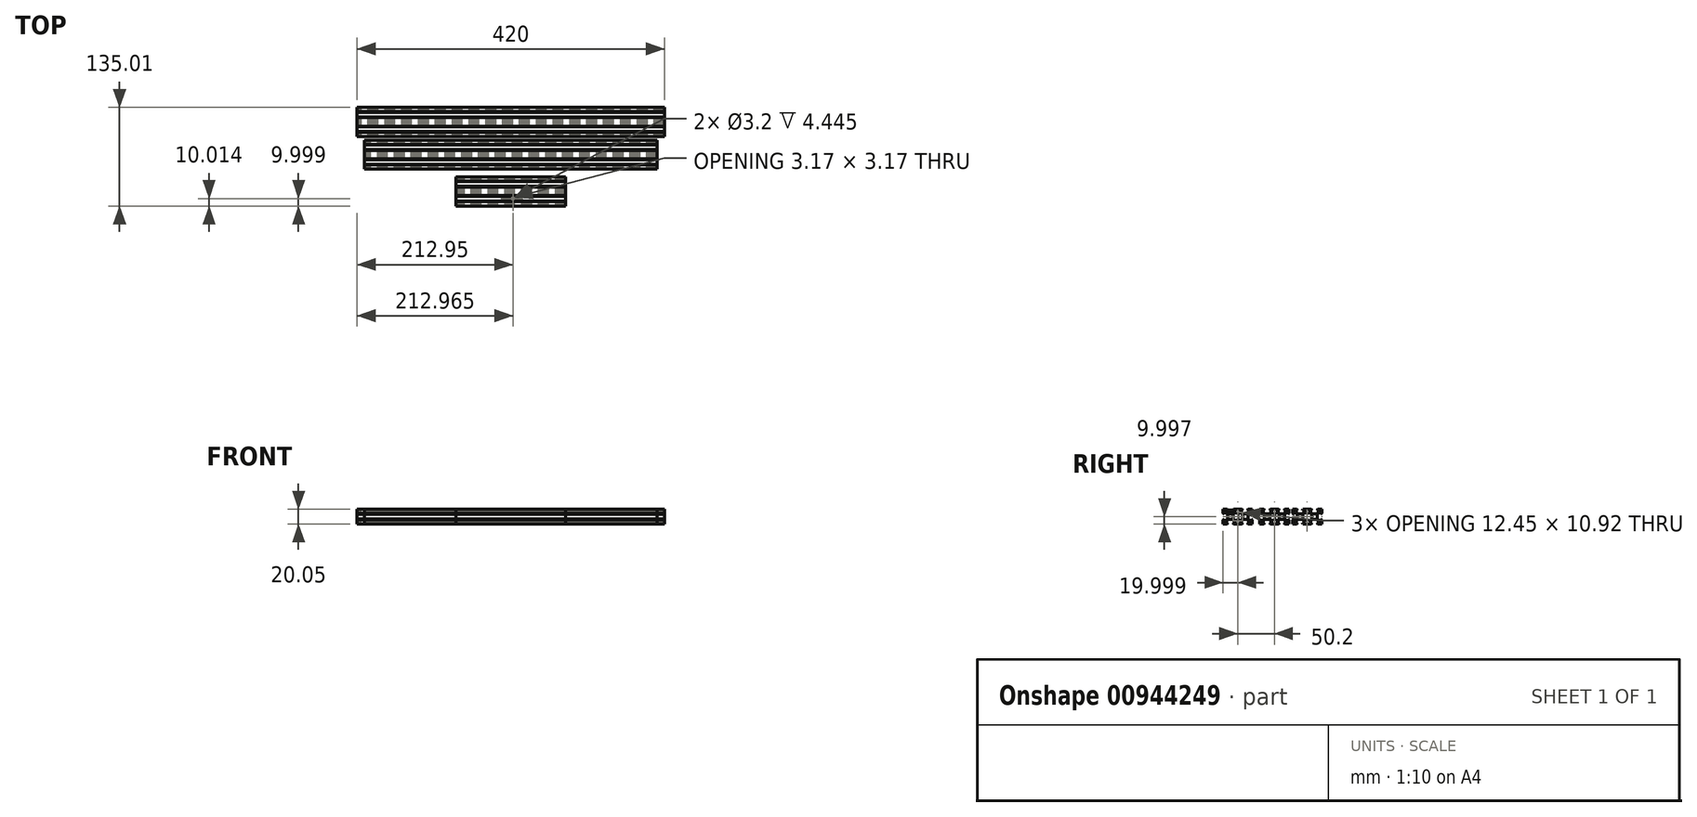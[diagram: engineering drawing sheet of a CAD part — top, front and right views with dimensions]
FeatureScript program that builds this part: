
annotation { "Feature Type Name" : "Feature", "Feature Type Description" : "" }
export const myFeature = defineFeature(function(context is Context, id is Id, definition is map)
    precondition{}
    {
        {
            var Q0;
            Q0=qCreatedBy(makeId("Right.planeOp"),FACE);
            var sketch = newSketch(context, id + "F0", { "sketchPlane" : qUnion([Q0])});
            skLineSegment(sketch, "E0.bottom", {"start": v(10.27, -9.71) * mm, "end": v(-9.73, -9.71) * mm});
            skLineSegment(sketch, "E0.top", {"start": v(10.27, 10.29) * mm, "end": v(-9.73, 10.29) * mm});
            skLineSegment(sketch, "E0.left", {"start": v(10.27, -9.71) * mm, "end": v(10.27, 10.29) * mm});
            skLineSegment(sketch, "E0.right", {"start": v(-9.73, -9.71) * mm, "end": v(-9.73, 10.29) * mm});
            skPoint(sketch, "E0.middle", {"position": v(0.27, 0.29) * mm});
            skLineSegment(sketch, "E1", {"start": v(4.51, 10.29) * mm, "end": v(3.38, 8.71) * mm});
            skLineSegment(sketch, "E2", {"start": v(3.38, 8.71) * mm, "end": v(3.38, 8.5) * mm});
            skLineSegment(sketch, "E3", {"start": v(3.38, 8.5) * mm, "end": v(5.73, 8.5) * mm});
            skLineSegment(sketch, "E4", {"start": v(5.73, 8.5) * mm, "end": v(5.73, 6.73) * mm});
            skLineSegment(sketch, "E5", {"start": v(5.73, 6.73) * mm, "end": v(3.38, 4.06) * mm});
            skLineSegment(sketch, "E6", {"start": v(3.38, 4.06) * mm, "end": v(0.27, 4.06) * mm});
            skLineSegment(sketch, "E7", {"start": v(0.27, 16.16) * mm, "end": v(0.27, -18.08) * mm, "construction": true});
            skPoint(sketch, "E7.endSnap0", {"position": v(0.27, -9.71) * mm});
            skLineSegment(sketch, "E8.0", {"start": v(5.73, 16.16) * mm, "end": v(5.73, -18.08) * mm, "construction": true});
            skLineSegment(sketch, "E9.MirrorCS", {"start": v(-3.98, 10.29) * mm, "end": v(-2.84, 8.71) * mm});
            skLineSegment(sketch, "E10.MirrorCS", {"start": v(-2.84, 8.71) * mm, "end": v(-2.84, 8.5) * mm});
            skLineSegment(sketch, "E11.MirrorCS", {"start": v(-2.84, 8.5) * mm, "end": v(-5.2, 8.5) * mm});
            skLineSegment(sketch, "E12.MirrorCS", {"start": v(-5.2, 16.16) * mm, "end": v(-5.2, -18.08) * mm, "construction": true});
            skLineSegment(sketch, "E13.MirrorCS", {"start": v(-5.2, 6.73) * mm, "end": v(-2.84, 4.06) * mm});
            skLineSegment(sketch, "E14.MirrorCS", {"start": v(-2.84, 4.06) * mm, "end": v(0.27, 4.06) * mm});
            skLineSegment(sketch, "E15.MirrorCS", {"start": v(-5.2, 8.5) * mm, "end": v(-5.2, 6.73) * mm});
            skLineSegment(sketch, "E16.1.0", {"start": v(-3.5, 3.4) * mm, "end": v(-3.5, 0.29) * mm});
            skLineSegment(sketch, "E16.1.1", {"start": v(-3.5, -2.82) * mm, "end": v(-3.5, 0.29) * mm});
            skLineSegment(sketch, "E16.1.2", {"start": v(-6.18, -5.17) * mm, "end": v(-3.5, -2.82) * mm});
            skLineSegment(sketch, "E16.1.3", {"start": v(-7.95, 3.4) * mm, "end": v(-7.95, 5.75) * mm});
            skLineSegment(sketch, "E16.1.4", {"start": v(-9.73, 4.53) * mm, "end": v(-8.16, 3.4) * mm});
            skLineSegment(sketch, "E16.1.5", {"start": v(-7.95, 5.75) * mm, "end": v(-6.18, 5.75) * mm});
            skLineSegment(sketch, "E16.1.6", {"start": v(-9.73, -3.96) * mm, "end": v(-8.16, -2.82) * mm});
            skLineSegment(sketch, "E16.1.7", {"start": v(-6.18, 5.75) * mm, "end": v(-3.5, 3.4) * mm});
            skLineSegment(sketch, "E16.1.8", {"start": v(-7.95, -5.17) * mm, "end": v(-6.18, -5.17) * mm});
            skLineSegment(sketch, "E16.1.9", {"start": v(-7.95, -2.82) * mm, "end": v(-7.95, -5.17) * mm});
            skLineSegment(sketch, "E16.1.10", {"start": v(-8.16, -2.82) * mm, "end": v(-7.95, -2.82) * mm});
            skLineSegment(sketch, "E16.1.11", {"start": v(-8.16, 3.4) * mm, "end": v(-7.95, 3.4) * mm});
            skLineSegment(sketch, "E16.2.0", {"start": v(-2.84, -3.5) * mm, "end": v(0.27, -3.5) * mm});
            skLineSegment(sketch, "E16.2.1", {"start": v(3.38, -3.5) * mm, "end": v(0.27, -3.5) * mm});
            skLineSegment(sketch, "E16.2.2", {"start": v(5.73, -6.16) * mm, "end": v(3.38, -3.5) * mm});
            skLineSegment(sketch, "E16.2.3", {"start": v(-2.84, -7.94) * mm, "end": v(-5.2, -7.94) * mm});
            skLineSegment(sketch, "E16.2.4", {"start": v(-3.98, -9.71) * mm, "end": v(-2.84, -8.14) * mm});
            skLineSegment(sketch, "E16.2.5", {"start": v(-5.2, -7.94) * mm, "end": v(-5.2, -6.16) * mm});
            skLineSegment(sketch, "E16.2.6", {"start": v(4.51, -9.71) * mm, "end": v(3.38, -8.14) * mm});
            skLineSegment(sketch, "E16.2.7", {"start": v(-5.2, -6.16) * mm, "end": v(-2.84, -3.5) * mm});
            skLineSegment(sketch, "E16.2.8", {"start": v(5.73, -7.94) * mm, "end": v(5.73, -6.16) * mm});
            skLineSegment(sketch, "E16.2.9", {"start": v(3.38, -7.94) * mm, "end": v(5.73, -7.94) * mm});
            skLineSegment(sketch, "E16.2.10", {"start": v(3.38, -8.14) * mm, "end": v(3.38, -7.94) * mm});
            skLineSegment(sketch, "E16.2.11", {"start": v(-2.84, -8.14) * mm, "end": v(-2.84, -7.94) * mm});
            skLineSegment(sketch, "E16.3.0", {"start": v(4.05, -2.82) * mm, "end": v(4.05, 0.29) * mm});
            skLineSegment(sketch, "E16.3.1", {"start": v(4.05, 3.4) * mm, "end": v(4.05, 0.29) * mm});
            skLineSegment(sketch, "E16.3.2", {"start": v(6.71, 5.75) * mm, "end": v(4.05, 3.4) * mm});
            skLineSegment(sketch, "E16.3.3", {"start": v(8.5, -2.82) * mm, "end": v(8.5, -5.17) * mm});
            skLineSegment(sketch, "E16.3.4", {"start": v(10.27, -3.96) * mm, "end": v(8.7, -2.82) * mm});
            skLineSegment(sketch, "E16.3.5", {"start": v(8.5, -5.17) * mm, "end": v(6.71, -5.17) * mm});
            skLineSegment(sketch, "E16.3.6", {"start": v(10.27, 4.53) * mm, "end": v(8.7, 3.4) * mm});
            skLineSegment(sketch, "E16.3.7", {"start": v(6.71, -5.17) * mm, "end": v(4.05, -2.82) * mm});
            skLineSegment(sketch, "E16.3.8", {"start": v(8.5, 5.75) * mm, "end": v(6.71, 5.75) * mm});
            skLineSegment(sketch, "E16.3.9", {"start": v(8.5, 3.4) * mm, "end": v(8.5, 5.75) * mm});
            skLineSegment(sketch, "E16.3.10", {"start": v(8.7, 3.4) * mm, "end": v(8.5, 3.4) * mm});
            skLineSegment(sketch, "E16.3.11", {"start": v(8.7, -2.82) * mm, "end": v(8.5, -2.82) * mm});
            skLineSegment(sketch, "E17.bottom", {"start": v(30.27, -9.71) * mm, "end": v(10.27, -9.71) * mm});
            skLineSegment(sketch, "E17.top", {"start": v(30.27, 10.29) * mm, "end": v(10.27, 10.29) * mm});
            skLineSegment(sketch, "E17.left", {"start": v(30.27, -9.71) * mm, "end": v(30.27, 10.29) * mm});
            skPoint(sketch, "E17.middle", {"position": v(20.27, 0.29) * mm});
            skLineSegment(sketch, "E18", {"start": v(24.51, 10.29) * mm, "end": v(23.38, 8.71) * mm});
            skLineSegment(sketch, "E19", {"start": v(23.38, 8.71) * mm, "end": v(23.38, 8.5) * mm});
            skLineSegment(sketch, "E20", {"start": v(23.38, 8.5) * mm, "end": v(25.73, 8.5) * mm});
            skLineSegment(sketch, "E21", {"start": v(25.73, 8.5) * mm, "end": v(25.73, 6.73) * mm});
            skLineSegment(sketch, "E22", {"start": v(25.73, 6.73) * mm, "end": v(23.38, 4.06) * mm});
            skLineSegment(sketch, "E23", {"start": v(23.38, 4.06) * mm, "end": v(20.27, 4.06) * mm});
            skPoint(sketch, "E24.endSnap0", {"position": v(20.27, -9.71) * mm});
            skLineSegment(sketch, "E25.MirrorCS", {"start": v(16.02, 10.29) * mm, "end": v(17.16, 8.71) * mm});
            skLineSegment(sketch, "E26.MirrorCS", {"start": v(17.16, 8.71) * mm, "end": v(17.16, 8.5) * mm});
            skLineSegment(sketch, "E27.MirrorCS", {"start": v(17.16, 8.5) * mm, "end": v(14.8, 8.5) * mm});
            skLineSegment(sketch, "E28.MirrorCS", {"start": v(14.8, 6.73) * mm, "end": v(17.16, 4.06) * mm});
            skLineSegment(sketch, "E29.MirrorCS", {"start": v(17.16, 4.06) * mm, "end": v(20.27, 4.06) * mm});
            skLineSegment(sketch, "E30.MirrorCS", {"start": v(14.8, 8.5) * mm, "end": v(14.8, 6.73) * mm});
            skLineSegment(sketch, "E31.1.0", {"start": v(16.5, 3.4) * mm, "end": v(16.5, 0.29) * mm});
            skLineSegment(sketch, "E31.1.1", {"start": v(16.5, -2.82) * mm, "end": v(16.5, 0.29) * mm});
            skLineSegment(sketch, "E31.1.2", {"start": v(13.82, -5.17) * mm, "end": v(16.5, -2.82) * mm});
            skLineSegment(sketch, "E31.1.3", {"start": v(12.05, 3.4) * mm, "end": v(12.05, 5.75) * mm});
            skLineSegment(sketch, "E31.1.4", {"start": v(10.27, 4.53) * mm, "end": v(11.84, 3.4) * mm});
            skLineSegment(sketch, "E31.1.5", {"start": v(12.05, 5.75) * mm, "end": v(13.82, 5.75) * mm});
            skLineSegment(sketch, "E31.1.6", {"start": v(10.27, -3.96) * mm, "end": v(11.84, -2.82) * mm});
            skLineSegment(sketch, "E31.1.7", {"start": v(13.82, 5.75) * mm, "end": v(16.5, 3.4) * mm});
            skLineSegment(sketch, "E31.1.8", {"start": v(12.05, -5.17) * mm, "end": v(13.82, -5.17) * mm});
            skLineSegment(sketch, "E31.1.9", {"start": v(12.05, -2.82) * mm, "end": v(12.05, -5.17) * mm});
            skLineSegment(sketch, "E31.1.10", {"start": v(11.84, -2.82) * mm, "end": v(12.05, -2.82) * mm});
            skLineSegment(sketch, "E31.1.11", {"start": v(11.84, 3.4) * mm, "end": v(12.05, 3.4) * mm});
            skLineSegment(sketch, "E31.2.0", {"start": v(17.16, -3.5) * mm, "end": v(20.27, -3.5) * mm});
            skLineSegment(sketch, "E31.2.1", {"start": v(23.38, -3.5) * mm, "end": v(20.27, -3.5) * mm});
            skLineSegment(sketch, "E31.2.2", {"start": v(25.73, -6.16) * mm, "end": v(23.38, -3.5) * mm});
            skLineSegment(sketch, "E31.2.3", {"start": v(17.16, -7.94) * mm, "end": v(14.8, -7.94) * mm});
            skLineSegment(sketch, "E31.2.4", {"start": v(16.02, -9.71) * mm, "end": v(17.16, -8.14) * mm});
            skLineSegment(sketch, "E31.2.5", {"start": v(14.8, -7.94) * mm, "end": v(14.8, -6.16) * mm});
            skLineSegment(sketch, "E31.2.6", {"start": v(24.51, -9.71) * mm, "end": v(23.38, -8.14) * mm});
            skLineSegment(sketch, "E31.2.7", {"start": v(14.8, -6.16) * mm, "end": v(17.16, -3.5) * mm});
            skLineSegment(sketch, "E31.2.8", {"start": v(25.73, -7.94) * mm, "end": v(25.73, -6.16) * mm});
            skLineSegment(sketch, "E31.2.9", {"start": v(23.38, -7.94) * mm, "end": v(25.73, -7.94) * mm});
            skLineSegment(sketch, "E31.2.10", {"start": v(23.38, -8.14) * mm, "end": v(23.38, -7.94) * mm});
            skLineSegment(sketch, "E31.2.11", {"start": v(17.16, -8.14) * mm, "end": v(17.16, -7.94) * mm});
            skLineSegment(sketch, "E31.3.0", {"start": v(24.05, -2.82) * mm, "end": v(24.05, 0.29) * mm});
            skLineSegment(sketch, "E31.3.1", {"start": v(24.05, 3.4) * mm, "end": v(24.05, 0.29) * mm});
            skLineSegment(sketch, "E31.3.2", {"start": v(26.71, 5.75) * mm, "end": v(24.05, 3.4) * mm});
            skLineSegment(sketch, "E31.3.3", {"start": v(28.5, -2.82) * mm, "end": v(28.5, -5.17) * mm});
            skLineSegment(sketch, "E31.3.4", {"start": v(30.27, -3.96) * mm, "end": v(28.7, -2.82) * mm});
            skLineSegment(sketch, "E31.3.5", {"start": v(28.5, -5.17) * mm, "end": v(26.71, -5.17) * mm});
            skLineSegment(sketch, "E31.3.6", {"start": v(30.27, 4.53) * mm, "end": v(28.7, 3.4) * mm});
            skLineSegment(sketch, "E31.3.7", {"start": v(26.71, -5.17) * mm, "end": v(24.05, -2.82) * mm});
            skLineSegment(sketch, "E31.3.8", {"start": v(28.5, 5.75) * mm, "end": v(26.71, 5.75) * mm});
            skLineSegment(sketch, "E31.3.9", {"start": v(28.5, 3.4) * mm, "end": v(28.5, 5.75) * mm});
            skLineSegment(sketch, "E31.3.10", {"start": v(28.7, 3.4) * mm, "end": v(28.5, 3.4) * mm});
            skLineSegment(sketch, "E31.3.11", {"start": v(28.7, -2.82) * mm, "end": v(28.5, -2.82) * mm});
            skSolve(sketch);
        }
        {
            var Q0;
            {var subQ11=sQuery(id+"F0.wireOp",EDGE,"E18");Q0=makeQuery(id+"F0.imprint","IMPRINT",FACE,{"disambiguationData":[TD([[makeQuery(id+"F0.imprint","IMPRINT",EDGE,{"derivedFrom":subQ11}),1.0]])]});}
            var Q1;
            {var subQ12=sQuery(id+"F0.wireOp",EDGE,"E1");Q1=makeQuery(id+"F0.imprint","IMPRINT",FACE,{"disambiguationData":[TD([[makeQuery(id+"F0.imprint","IMPRINT",EDGE,{"derivedFrom":subQ12}),1.0]])]});}
            extrude(context, id + "F1", {"entities" : qUnion([Q0, Q1]), "depth" : 420 * mm, "symmetric" : true});
        }
        {
            var Q0;
            Q0=qCreatedBy(makeId("Right.planeOp"),FACE);
            var sketch = newSketch(context, id + "F2", { "sketchPlane" : qUnion([Q0])});
            skLineSegment(sketch, "E32.bottom", {"start": v(0.66, -9.76) * mm, "end": v(-19.34, -9.76) * mm});
            skLineSegment(sketch, "E32.top", {"start": v(0.66, 10.24) * mm, "end": v(-19.34, 10.24) * mm});
            skLineSegment(sketch, "E32.left", {"start": v(0.66, -9.76) * mm, "end": v(0.66, 10.24) * mm});
            skLineSegment(sketch, "E32.right", {"start": v(-19.34, -9.76) * mm, "end": v(-19.34, 10.24) * mm});
            skPoint(sketch, "E32.middle", {"position": v(-9.34, 0.24) * mm});
            skLineSegment(sketch, "E33", {"start": v(-5.1, 10.24) * mm, "end": v(-6.23, 8.66) * mm});
            skLineSegment(sketch, "E34", {"start": v(-6.23, 8.66) * mm, "end": v(-6.23, 8.46) * mm});
            skLineSegment(sketch, "E35", {"start": v(-6.23, 8.46) * mm, "end": v(-3.88, 8.46) * mm});
            skLineSegment(sketch, "E36", {"start": v(-3.88, 8.46) * mm, "end": v(-3.88, 6.68) * mm});
            skLineSegment(sketch, "E37", {"start": v(-3.88, 6.68) * mm, "end": v(-6.23, 4.01) * mm});
            skLineSegment(sketch, "E38", {"start": v(-6.23, 4.01) * mm, "end": v(-9.34, 4.01) * mm});
            skLineSegment(sketch, "E39", {"start": v(-9.34, 16.11) * mm, "end": v(-9.34, -18.13) * mm, "construction": true});
            skPoint(sketch, "E39.endSnap0", {"position": v(-9.34, -9.76) * mm});
            skLineSegment(sketch, "E40.0", {"start": v(-3.88, 16.11) * mm, "end": v(-3.88, -18.13) * mm, "construction": true});
            skLineSegment(sketch, "E41.MirrorCS", {"start": v(-13.59, 10.24) * mm, "end": v(-12.45, 8.66) * mm});
            skLineSegment(sketch, "E42.MirrorCS", {"start": v(-12.45, 8.66) * mm, "end": v(-12.45, 8.46) * mm});
            skLineSegment(sketch, "E43.MirrorCS", {"start": v(-12.45, 8.46) * mm, "end": v(-14.8, 8.46) * mm});
            skLineSegment(sketch, "E44.MirrorCS", {"start": v(-14.8, 16.11) * mm, "end": v(-14.8, -18.13) * mm, "construction": true});
            skLineSegment(sketch, "E45.MirrorCS", {"start": v(-14.8, 6.68) * mm, "end": v(-12.45, 4.01) * mm});
            skLineSegment(sketch, "E46.MirrorCS", {"start": v(-12.45, 4.01) * mm, "end": v(-9.34, 4.01) * mm});
            skLineSegment(sketch, "E47.MirrorCS", {"start": v(-14.8, 8.46) * mm, "end": v(-14.8, 6.68) * mm});
            skLineSegment(sketch, "E48.1.0", {"start": v(-13.12, 3.35) * mm, "end": v(-13.12, 0.24) * mm});
            skLineSegment(sketch, "E48.1.1", {"start": v(-13.12, -2.87) * mm, "end": v(-13.12, 0.24) * mm});
            skLineSegment(sketch, "E48.1.2", {"start": v(-15.79, -5.22) * mm, "end": v(-13.12, -2.87) * mm});
            skLineSegment(sketch, "E48.1.3", {"start": v(-17.56, 3.35) * mm, "end": v(-17.56, 5.7) * mm});
            skLineSegment(sketch, "E48.1.4", {"start": v(-19.34, 4.48) * mm, "end": v(-17.77, 3.35) * mm});
            skLineSegment(sketch, "E48.1.5", {"start": v(-17.56, 5.7) * mm, "end": v(-15.79, 5.7) * mm});
            skLineSegment(sketch, "E48.1.6", {"start": v(-19.34, -4) * mm, "end": v(-17.77, -2.87) * mm});
            skLineSegment(sketch, "E48.1.7", {"start": v(-15.79, 5.7) * mm, "end": v(-13.12, 3.35) * mm});
            skLineSegment(sketch, "E48.1.8", {"start": v(-17.56, -5.22) * mm, "end": v(-15.79, -5.22) * mm});
            skLineSegment(sketch, "E48.1.9", {"start": v(-17.56, -2.87) * mm, "end": v(-17.56, -5.22) * mm});
            skLineSegment(sketch, "E48.1.10", {"start": v(-17.77, -2.87) * mm, "end": v(-17.56, -2.87) * mm});
            skLineSegment(sketch, "E48.1.11", {"start": v(-17.77, 3.35) * mm, "end": v(-17.56, 3.35) * mm});
            skLineSegment(sketch, "E48.2.0", {"start": v(-12.45, -3.54) * mm, "end": v(-9.34, -3.54) * mm});
            skLineSegment(sketch, "E48.2.1", {"start": v(-6.23, -3.54) * mm, "end": v(-9.34, -3.54) * mm});
            skLineSegment(sketch, "E48.2.2", {"start": v(-3.88, -6.2) * mm, "end": v(-6.23, -3.54) * mm});
            skLineSegment(sketch, "E48.2.3", {"start": v(-12.45, -7.98) * mm, "end": v(-14.8, -7.98) * mm});
            skLineSegment(sketch, "E48.2.4", {"start": v(-13.59, -9.76) * mm, "end": v(-12.45, -8.19) * mm});
            skLineSegment(sketch, "E48.2.5", {"start": v(-14.8, -7.98) * mm, "end": v(-14.8, -6.2) * mm});
            skLineSegment(sketch, "E48.2.6", {"start": v(-5.1, -9.76) * mm, "end": v(-6.23, -8.19) * mm});
            skLineSegment(sketch, "E48.2.7", {"start": v(-14.8, -6.2) * mm, "end": v(-12.45, -3.54) * mm});
            skLineSegment(sketch, "E48.2.8", {"start": v(-3.88, -7.98) * mm, "end": v(-3.88, -6.2) * mm});
            skLineSegment(sketch, "E48.2.9", {"start": v(-6.23, -7.98) * mm, "end": v(-3.88, -7.98) * mm});
            skLineSegment(sketch, "E48.2.10", {"start": v(-6.23, -8.19) * mm, "end": v(-6.23, -7.98) * mm});
            skLineSegment(sketch, "E48.2.11", {"start": v(-12.45, -8.19) * mm, "end": v(-12.45, -7.98) * mm});
            skLineSegment(sketch, "E48.3.0", {"start": v(-5.56, -2.87) * mm, "end": v(-5.56, 0.24) * mm});
            skLineSegment(sketch, "E48.3.1", {"start": v(-5.56, 3.35) * mm, "end": v(-5.56, 0.24) * mm});
            skLineSegment(sketch, "E48.3.2", {"start": v(-2.9, 5.7) * mm, "end": v(-5.56, 3.35) * mm});
            skLineSegment(sketch, "E48.3.3", {"start": v(-1.12, -2.87) * mm, "end": v(-1.12, -5.22) * mm});
            skLineSegment(sketch, "E48.3.4", {"start": v(0.66, -4) * mm, "end": v(-0.92, -2.87) * mm});
            skLineSegment(sketch, "E48.3.5", {"start": v(-1.12, -5.22) * mm, "end": v(-2.9, -5.22) * mm});
            skLineSegment(sketch, "E48.3.6", {"start": v(0.66, 4.48) * mm, "end": v(-0.92, 3.35) * mm});
            skLineSegment(sketch, "E48.3.7", {"start": v(-2.9, -5.22) * mm, "end": v(-5.56, -2.87) * mm});
            skLineSegment(sketch, "E48.3.8", {"start": v(-1.12, 5.7) * mm, "end": v(-2.9, 5.7) * mm});
            skLineSegment(sketch, "E48.3.9", {"start": v(-1.12, 3.35) * mm, "end": v(-1.12, 5.7) * mm});
            skLineSegment(sketch, "E48.3.10", {"start": v(-0.92, 3.35) * mm, "end": v(-1.12, 3.35) * mm});
            skLineSegment(sketch, "E48.3.11", {"start": v(-0.92, -2.87) * mm, "end": v(-1.12, -2.87) * mm});
            skLineSegment(sketch, "E49.bottom", {"start": v(20.66, -9.76) * mm, "end": v(0.66, -9.76) * mm});
            skLineSegment(sketch, "E49.top", {"start": v(20.66, 10.24) * mm, "end": v(0.66, 10.24) * mm});
            skLineSegment(sketch, "E49.left", {"start": v(20.66, -9.76) * mm, "end": v(20.66, 10.24) * mm});
            skPoint(sketch, "E49.middle", {"position": v(10.66, 0.24) * mm});
            skLineSegment(sketch, "E50", {"start": v(14.9, 10.24) * mm, "end": v(13.77, 8.66) * mm});
            skLineSegment(sketch, "E51", {"start": v(13.77, 8.66) * mm, "end": v(13.77, 8.46) * mm});
            skLineSegment(sketch, "E52", {"start": v(13.77, 8.46) * mm, "end": v(16.12, 8.46) * mm});
            skLineSegment(sketch, "E53", {"start": v(16.12, 8.46) * mm, "end": v(16.12, 6.68) * mm});
            skLineSegment(sketch, "E54", {"start": v(16.12, 6.68) * mm, "end": v(13.77, 4.01) * mm});
            skLineSegment(sketch, "E55", {"start": v(13.77, 4.01) * mm, "end": v(10.66, 4.01) * mm});
            skPoint(sketch, "E56.endSnap0", {"position": v(10.66, -9.76) * mm});
            skLineSegment(sketch, "E57.MirrorCS", {"start": v(6.41, 10.24) * mm, "end": v(7.55, 8.66) * mm});
            skLineSegment(sketch, "E58.MirrorCS", {"start": v(7.55, 8.66) * mm, "end": v(7.55, 8.46) * mm});
            skLineSegment(sketch, "E59.MirrorCS", {"start": v(7.55, 8.46) * mm, "end": v(5.2, 8.46) * mm});
            skLineSegment(sketch, "E60.MirrorCS", {"start": v(5.2, 6.68) * mm, "end": v(7.55, 4.01) * mm});
            skLineSegment(sketch, "E61.MirrorCS", {"start": v(7.55, 4.01) * mm, "end": v(10.66, 4.01) * mm});
            skLineSegment(sketch, "E62.MirrorCS", {"start": v(5.2, 8.46) * mm, "end": v(5.2, 6.68) * mm});
            skLineSegment(sketch, "E63.1.0", {"start": v(6.88, 3.35) * mm, "end": v(6.88, 0.24) * mm});
            skLineSegment(sketch, "E63.1.1", {"start": v(6.88, -2.87) * mm, "end": v(6.88, 0.24) * mm});
            skLineSegment(sketch, "E63.1.2", {"start": v(4.21, -5.22) * mm, "end": v(6.88, -2.87) * mm});
            skLineSegment(sketch, "E63.1.3", {"start": v(2.44, 3.35) * mm, "end": v(2.44, 5.7) * mm});
            skLineSegment(sketch, "E63.1.4", {"start": v(0.66, 4.48) * mm, "end": v(2.23, 3.35) * mm});
            skLineSegment(sketch, "E63.1.5", {"start": v(2.44, 5.7) * mm, "end": v(4.21, 5.7) * mm});
            skLineSegment(sketch, "E63.1.6", {"start": v(0.66, -4) * mm, "end": v(2.23, -2.87) * mm});
            skLineSegment(sketch, "E63.1.7", {"start": v(4.21, 5.7) * mm, "end": v(6.88, 3.35) * mm});
            skLineSegment(sketch, "E63.1.8", {"start": v(2.44, -5.22) * mm, "end": v(4.21, -5.22) * mm});
            skLineSegment(sketch, "E63.1.9", {"start": v(2.44, -2.87) * mm, "end": v(2.44, -5.22) * mm});
            skLineSegment(sketch, "E63.1.10", {"start": v(2.23, -2.87) * mm, "end": v(2.44, -2.87) * mm});
            skLineSegment(sketch, "E63.1.11", {"start": v(2.23, 3.35) * mm, "end": v(2.44, 3.35) * mm});
            skLineSegment(sketch, "E63.2.0", {"start": v(7.55, -3.54) * mm, "end": v(10.66, -3.54) * mm});
            skLineSegment(sketch, "E63.2.1", {"start": v(13.77, -3.54) * mm, "end": v(10.66, -3.54) * mm});
            skLineSegment(sketch, "E63.2.2", {"start": v(16.12, -6.2) * mm, "end": v(13.77, -3.54) * mm});
            skLineSegment(sketch, "E63.2.3", {"start": v(7.55, -7.98) * mm, "end": v(5.2, -7.98) * mm});
            skLineSegment(sketch, "E63.2.4", {"start": v(6.41, -9.76) * mm, "end": v(7.55, -8.19) * mm});
            skLineSegment(sketch, "E63.2.5", {"start": v(5.2, -7.98) * mm, "end": v(5.2, -6.2) * mm});
            skLineSegment(sketch, "E63.2.6", {"start": v(14.9, -9.76) * mm, "end": v(13.77, -8.19) * mm});
            skLineSegment(sketch, "E63.2.7", {"start": v(5.2, -6.2) * mm, "end": v(7.55, -3.54) * mm});
            skLineSegment(sketch, "E63.2.8", {"start": v(16.12, -7.98) * mm, "end": v(16.12, -6.2) * mm});
            skLineSegment(sketch, "E63.2.9", {"start": v(13.77, -7.98) * mm, "end": v(16.12, -7.98) * mm});
            skLineSegment(sketch, "E63.2.10", {"start": v(13.77, -8.19) * mm, "end": v(13.77, -7.98) * mm});
            skLineSegment(sketch, "E63.2.11", {"start": v(7.55, -8.19) * mm, "end": v(7.55, -7.98) * mm});
            skLineSegment(sketch, "E63.3.0", {"start": v(14.44, -2.87) * mm, "end": v(14.44, 0.24) * mm});
            skLineSegment(sketch, "E63.3.1", {"start": v(14.44, 3.35) * mm, "end": v(14.44, 0.24) * mm});
            skLineSegment(sketch, "E63.3.2", {"start": v(17.1, 5.7) * mm, "end": v(14.44, 3.35) * mm});
            skLineSegment(sketch, "E63.3.3", {"start": v(18.88, -2.87) * mm, "end": v(18.88, -5.22) * mm});
            skLineSegment(sketch, "E63.3.4", {"start": v(20.66, -4) * mm, "end": v(19.08, -2.87) * mm});
            skLineSegment(sketch, "E63.3.5", {"start": v(18.88, -5.22) * mm, "end": v(17.1, -5.22) * mm});
            skLineSegment(sketch, "E63.3.6", {"start": v(20.66, 4.48) * mm, "end": v(19.08, 3.35) * mm});
            skLineSegment(sketch, "E63.3.7", {"start": v(17.1, -5.22) * mm, "end": v(14.44, -2.87) * mm});
            skLineSegment(sketch, "E63.3.8", {"start": v(18.88, 5.7) * mm, "end": v(17.1, 5.7) * mm});
            skLineSegment(sketch, "E63.3.9", {"start": v(18.88, 3.35) * mm, "end": v(18.88, 5.7) * mm});
            skLineSegment(sketch, "E63.3.10", {"start": v(19.08, 3.35) * mm, "end": v(18.88, 3.35) * mm});
            skLineSegment(sketch, "E63.3.11", {"start": v(19.08, -2.87) * mm, "end": v(18.88, -2.87) * mm});
            skSolve(sketch);
        }
        {
            var Q0;
            Q0=makeQuery(id+"F1.opExtrude","SWEPT_BODY",BODY,{"disambiguationData":[OSD([sQuery(id+"F0.wireOp",EDGE,"E0.bottom"),sQuery(id+"F0.wireOp",EDGE,"E0.top"),sQuery(id+"F0.wireOp",EDGE,"E0.right"),sQuery(id+"F0.wireOp",EDGE,"E1"),sQuery(id+"F0.wireOp",EDGE,"E2"),sQuery(id+"F0.wireOp",EDGE,"E3"),sQuery(id+"F0.wireOp",EDGE,"E4"),sQuery(id+"F0.wireOp",EDGE,"E5"),sQuery(id+"F0.wireOp",EDGE,"E6"),sQuery(id+"F0.wireOp",EDGE,"E9.MirrorCS"),sQuery(id+"F0.wireOp",EDGE,"E10.MirrorCS"),sQuery(id+"F0.wireOp",EDGE,"E11.MirrorCS"),sQuery(id+"F0.wireOp",EDGE,"E13.MirrorCS"),sQuery(id+"F0.wireOp",EDGE,"E14.MirrorCS"),sQuery(id+"F0.wireOp",EDGE,"E15.MirrorCS"),sQuery(id+"F0.wireOp",EDGE,"E16.1.0"),sQuery(id+"F0.wireOp",EDGE,"E16.1.1"),sQuery(id+"F0.wireOp",EDGE,"E16.1.2"),sQuery(id+"F0.wireOp",EDGE,"E16.1.3"),sQuery(id+"F0.wireOp",EDGE,"E16.1.4"),sQuery(id+"F0.wireOp",EDGE,"E16.1.5"),sQuery(id+"F0.wireOp",EDGE,"E16.1.6"),sQuery(id+"F0.wireOp",EDGE,"E16.1.7"),sQuery(id+"F0.wireOp",EDGE,"E16.1.8"),sQuery(id+"F0.wireOp",EDGE,"E16.1.9"),sQuery(id+"F0.wireOp",EDGE,"E16.1.10"),sQuery(id+"F0.wireOp",EDGE,"E16.1.11"),sQuery(id+"F0.wireOp",EDGE,"E16.2.0"),sQuery(id+"F0.wireOp",EDGE,"E16.2.1"),sQuery(id+"F0.wireOp",EDGE,"E16.2.2"),sQuery(id+"F0.wireOp",EDGE,"E16.2.3"),sQuery(id+"F0.wireOp",EDGE,"E16.2.4"),sQuery(id+"F0.wireOp",EDGE,"E16.2.5"),sQuery(id+"F0.wireOp",EDGE,"E16.2.6"),sQuery(id+"F0.wireOp",EDGE,"E16.2.7"),sQuery(id+"F0.wireOp",EDGE,"E16.2.8"),sQuery(id+"F0.wireOp",EDGE,"E16.2.9"),sQuery(id+"F0.wireOp",EDGE,"E16.2.10"),sQuery(id+"F0.wireOp",EDGE,"E16.2.11"),sQuery(id+"F0.wireOp",EDGE,"E16.3.0"),sQuery(id+"F0.wireOp",EDGE,"E16.3.1"),sQuery(id+"F0.wireOp",EDGE,"E16.3.2"),sQuery(id+"F0.wireOp",EDGE,"E16.3.3"),sQuery(id+"F0.wireOp",EDGE,"E16.3.4"),sQuery(id+"F0.wireOp",EDGE,"E16.3.5"),sQuery(id+"F0.wireOp",EDGE,"E16.3.6"),sQuery(id+"F0.wireOp",EDGE,"E16.3.7"),sQuery(id+"F0.wireOp",EDGE,"E16.3.8"),sQuery(id+"F0.wireOp",EDGE,"E16.3.9"),sQuery(id+"F0.wireOp",EDGE,"E16.3.10"),sQuery(id+"F0.wireOp",EDGE,"E16.3.11"),sQuery(id+"F0.wireOp",EDGE,"E17.bottom"),sQuery(id+"F0.wireOp",EDGE,"E17.top"),sQuery(id+"F0.wireOp",EDGE,"E17.left"),sQuery(id+"F0.wireOp",EDGE,"E18"),sQuery(id+"F0.wireOp",EDGE,"E19"),sQuery(id+"F0.wireOp",EDGE,"E20"),sQuery(id+"F0.wireOp",EDGE,"E21"),sQuery(id+"F0.wireOp",EDGE,"E22"),sQuery(id+"F0.wireOp",EDGE,"E23"),sQuery(id+"F0.wireOp",EDGE,"E25.MirrorCS"),sQuery(id+"F0.wireOp",EDGE,"E26.MirrorCS"),sQuery(id+"F0.wireOp",EDGE,"E27.MirrorCS"),sQuery(id+"F0.wireOp",EDGE,"E28.MirrorCS"),sQuery(id+"F0.wireOp",EDGE,"E29.MirrorCS"),sQuery(id+"F0.wireOp",EDGE,"E30.MirrorCS"),sQuery(id+"F0.wireOp",EDGE,"E31.1.0"),sQuery(id+"F0.wireOp",EDGE,"E31.1.1"),sQuery(id+"F0.wireOp",EDGE,"E31.1.2"),sQuery(id+"F0.wireOp",EDGE,"E31.1.3"),sQuery(id+"F0.wireOp",EDGE,"E31.1.4"),sQuery(id+"F0.wireOp",EDGE,"E31.1.5"),sQuery(id+"F0.wireOp",EDGE,"E31.1.6"),sQuery(id+"F0.wireOp",EDGE,"E31.1.7"),sQuery(id+"F0.wireOp",EDGE,"E31.1.8"),sQuery(id+"F0.wireOp",EDGE,"E31.1.9"),sQuery(id+"F0.wireOp",EDGE,"E31.1.10"),sQuery(id+"F0.wireOp",EDGE,"E31.1.11"),sQuery(id+"F0.wireOp",EDGE,"E31.2.0"),sQuery(id+"F0.wireOp",EDGE,"E31.2.1"),sQuery(id+"F0.wireOp",EDGE,"E31.2.2"),sQuery(id+"F0.wireOp",EDGE,"E31.2.3"),sQuery(id+"F0.wireOp",EDGE,"E31.2.4"),sQuery(id+"F0.wireOp",EDGE,"E31.2.5"),sQuery(id+"F0.wireOp",EDGE,"E31.2.6"),sQuery(id+"F0.wireOp",EDGE,"E31.2.7"),sQuery(id+"F0.wireOp",EDGE,"E31.2.8"),sQuery(id+"F0.wireOp",EDGE,"E31.2.9"),sQuery(id+"F0.wireOp",EDGE,"E31.2.10"),sQuery(id+"F0.wireOp",EDGE,"E31.2.11"),sQuery(id+"F0.wireOp",EDGE,"E31.3.0"),sQuery(id+"F0.wireOp",EDGE,"E31.3.1"),sQuery(id+"F0.wireOp",EDGE,"E31.3.2"),sQuery(id+"F0.wireOp",EDGE,"E31.3.3"),sQuery(id+"F0.wireOp",EDGE,"E31.3.4"),sQuery(id+"F0.wireOp",EDGE,"E31.3.5"),sQuery(id+"F0.wireOp",EDGE,"E31.3.6"),sQuery(id+"F0.wireOp",EDGE,"E31.3.7"),sQuery(id+"F0.wireOp",EDGE,"E31.3.8"),sQuery(id+"F0.wireOp",EDGE,"E31.3.9"),sQuery(id+"F0.wireOp",EDGE,"E31.3.10"),sQuery(id+"F0.wireOp",EDGE,"E31.3.11")])]});
            transform(context, id + "F3", {"entities" : qUnion([Q0]), "transformType" : TransformType.TRANSLATION_3D, "dx" : 0 * mm, "dy" : 35.2 * mm, "dz" : 0 * mm, "makeCopy" : false});
        }
        {
            var Q0;
            {var subQ12=sQuery(id+"F2.wireOp",EDGE,"E33");Q0=makeQuery(id+"F2.imprint","IMPRINT",FACE,{"disambiguationData":[TD([[makeQuery(id+"F2.imprint","IMPRINT",EDGE,{"derivedFrom":subQ12}),1.0]])]});}
            var Q1;
            {var subQ4=sQuery(id+"F2.wireOp",EDGE,"E50");Q1=makeQuery(id+"F2.imprint","IMPRINT",FACE,{"disambiguationData":[TD([[makeQuery(id+"F2.imprint","IMPRINT",EDGE,{"derivedFrom":subQ4}),1.0]])]});}
            extrude(context, id + "F4", {"entities" : qUnion([Q0, Q1]), "depth" : 150 * mm, "symmetric" : true});
        }
        {
            var Q0;
            Q0=makeQuery(id+"F4.opExtrude","SWEPT_BODY",BODY,{"disambiguationData":[OSD([sQuery(id+"F2.wireOp",EDGE,"E32.bottom"),sQuery(id+"F2.wireOp",EDGE,"E32.top"),sQuery(id+"F2.wireOp",EDGE,"E32.right"),sQuery(id+"F2.wireOp",EDGE,"E33"),sQuery(id+"F2.wireOp",EDGE,"E34"),sQuery(id+"F2.wireOp",EDGE,"E35"),sQuery(id+"F2.wireOp",EDGE,"E36"),sQuery(id+"F2.wireOp",EDGE,"E37"),sQuery(id+"F2.wireOp",EDGE,"E38"),sQuery(id+"F2.wireOp",EDGE,"E41.MirrorCS"),sQuery(id+"F2.wireOp",EDGE,"E42.MirrorCS"),sQuery(id+"F2.wireOp",EDGE,"E43.MirrorCS"),sQuery(id+"F2.wireOp",EDGE,"E45.MirrorCS"),sQuery(id+"F2.wireOp",EDGE,"E46.MirrorCS"),sQuery(id+"F2.wireOp",EDGE,"E47.MirrorCS"),sQuery(id+"F2.wireOp",EDGE,"E48.1.0"),sQuery(id+"F2.wireOp",EDGE,"E48.1.1"),sQuery(id+"F2.wireOp",EDGE,"E48.1.2"),sQuery(id+"F2.wireOp",EDGE,"E48.1.3"),sQuery(id+"F2.wireOp",EDGE,"E48.1.4"),sQuery(id+"F2.wireOp",EDGE,"E48.1.5"),sQuery(id+"F2.wireOp",EDGE,"E48.1.6"),sQuery(id+"F2.wireOp",EDGE,"E48.1.7"),sQuery(id+"F2.wireOp",EDGE,"E48.1.8"),sQuery(id+"F2.wireOp",EDGE,"E48.1.9"),sQuery(id+"F2.wireOp",EDGE,"E48.1.10"),sQuery(id+"F2.wireOp",EDGE,"E48.1.11"),sQuery(id+"F2.wireOp",EDGE,"E48.2.0"),sQuery(id+"F2.wireOp",EDGE,"E48.2.1"),sQuery(id+"F2.wireOp",EDGE,"E48.2.2"),sQuery(id+"F2.wireOp",EDGE,"E48.2.3"),sQuery(id+"F2.wireOp",EDGE,"E48.2.4"),sQuery(id+"F2.wireOp",EDGE,"E48.2.5"),sQuery(id+"F2.wireOp",EDGE,"E48.2.6"),sQuery(id+"F2.wireOp",EDGE,"E48.2.7"),sQuery(id+"F2.wireOp",EDGE,"E48.2.8"),sQuery(id+"F2.wireOp",EDGE,"E48.2.9"),sQuery(id+"F2.wireOp",EDGE,"E48.2.10"),sQuery(id+"F2.wireOp",EDGE,"E48.2.11"),sQuery(id+"F2.wireOp",EDGE,"E48.3.0"),sQuery(id+"F2.wireOp",EDGE,"E48.3.1"),sQuery(id+"F2.wireOp",EDGE,"E48.3.2"),sQuery(id+"F2.wireOp",EDGE,"E48.3.3"),sQuery(id+"F2.wireOp",EDGE,"E48.3.4"),sQuery(id+"F2.wireOp",EDGE,"E48.3.5"),sQuery(id+"F2.wireOp",EDGE,"E48.3.6"),sQuery(id+"F2.wireOp",EDGE,"E48.3.7"),sQuery(id+"F2.wireOp",EDGE,"E48.3.8"),sQuery(id+"F2.wireOp",EDGE,"E48.3.9"),sQuery(id+"F2.wireOp",EDGE,"E48.3.10"),sQuery(id+"F2.wireOp",EDGE,"E48.3.11"),sQuery(id+"F2.wireOp",EDGE,"E49.bottom"),sQuery(id+"F2.wireOp",EDGE,"E49.top"),sQuery(id+"F2.wireOp",EDGE,"E49.left"),sQuery(id+"F2.wireOp",EDGE,"E50"),sQuery(id+"F2.wireOp",EDGE,"E51"),sQuery(id+"F2.wireOp",EDGE,"E52"),sQuery(id+"F2.wireOp",EDGE,"E53"),sQuery(id+"F2.wireOp",EDGE,"E54"),sQuery(id+"F2.wireOp",EDGE,"E55"),sQuery(id+"F2.wireOp",EDGE,"E57.MirrorCS"),sQuery(id+"F2.wireOp",EDGE,"E58.MirrorCS"),sQuery(id+"F2.wireOp",EDGE,"E59.MirrorCS"),sQuery(id+"F2.wireOp",EDGE,"E60.MirrorCS"),sQuery(id+"F2.wireOp",EDGE,"E61.MirrorCS"),sQuery(id+"F2.wireOp",EDGE,"E62.MirrorCS"),sQuery(id+"F2.wireOp",EDGE,"E63.1.0"),sQuery(id+"F2.wireOp",EDGE,"E63.1.1"),sQuery(id+"F2.wireOp",EDGE,"E63.1.2"),sQuery(id+"F2.wireOp",EDGE,"E63.1.3"),sQuery(id+"F2.wireOp",EDGE,"E63.1.4"),sQuery(id+"F2.wireOp",EDGE,"E63.1.5"),sQuery(id+"F2.wireOp",EDGE,"E63.1.6"),sQuery(id+"F2.wireOp",EDGE,"E63.1.7"),sQuery(id+"F2.wireOp",EDGE,"E63.1.8"),sQuery(id+"F2.wireOp",EDGE,"E63.1.9"),sQuery(id+"F2.wireOp",EDGE,"E63.1.10"),sQuery(id+"F2.wireOp",EDGE,"E63.1.11"),sQuery(id+"F2.wireOp",EDGE,"E63.2.0"),sQuery(id+"F2.wireOp",EDGE,"E63.2.1"),sQuery(id+"F2.wireOp",EDGE,"E63.2.2"),sQuery(id+"F2.wireOp",EDGE,"E63.2.3"),sQuery(id+"F2.wireOp",EDGE,"E63.2.4"),sQuery(id+"F2.wireOp",EDGE,"E63.2.5"),sQuery(id+"F2.wireOp",EDGE,"E63.2.6"),sQuery(id+"F2.wireOp",EDGE,"E63.2.7"),sQuery(id+"F2.wireOp",EDGE,"E63.2.8"),sQuery(id+"F2.wireOp",EDGE,"E63.2.9"),sQuery(id+"F2.wireOp",EDGE,"E63.2.10"),sQuery(id+"F2.wireOp",EDGE,"E63.2.11"),sQuery(id+"F2.wireOp",EDGE,"E63.3.0"),sQuery(id+"F2.wireOp",EDGE,"E63.3.1"),sQuery(id+"F2.wireOp",EDGE,"E63.3.2"),sQuery(id+"F2.wireOp",EDGE,"E63.3.3"),sQuery(id+"F2.wireOp",EDGE,"E63.3.4"),sQuery(id+"F2.wireOp",EDGE,"E63.3.5"),sQuery(id+"F2.wireOp",EDGE,"E63.3.6"),sQuery(id+"F2.wireOp",EDGE,"E63.3.7"),sQuery(id+"F2.wireOp",EDGE,"E63.3.8"),sQuery(id+"F2.wireOp",EDGE,"E63.3.9"),sQuery(id+"F2.wireOp",EDGE,"E63.3.10"),sQuery(id+"F2.wireOp",EDGE,"E63.3.11")])]});
            transform(context, id + "F5", {"entities" : qUnion([Q0]), "transformType" : TransformType.TRANSLATION_3D, "dx" : 0 * mm, "dy" : -50.2 * mm, "dz" : 0 * mm, "makeCopy" : false});
        }
        {
            var Q0;
            Q0=qCreatedBy(makeId("Right.planeOp"),FACE);
            var sketch = newSketch(context, id + "F6", { "sketchPlane" : qUnion([Q0])});
            skLineSegment(sketch, "E64.bottom", {"start": v(0.66, -9.76) * mm, "end": v(-19.34, -9.76) * mm});
            skLineSegment(sketch, "E64.top", {"start": v(0.66, 10.24) * mm, "end": v(-19.34, 10.24) * mm});
            skLineSegment(sketch, "E64.left", {"start": v(0.66, -9.76) * mm, "end": v(0.66, 10.24) * mm});
            skLineSegment(sketch, "E64.right", {"start": v(-19.34, -9.76) * mm, "end": v(-19.34, 10.24) * mm});
            skPoint(sketch, "E64.middle", {"position": v(-9.34, 0.24) * mm});
            skLineSegment(sketch, "E65", {"start": v(-5.1, 10.24) * mm, "end": v(-6.23, 8.66) * mm});
            skLineSegment(sketch, "E66", {"start": v(-6.23, 8.66) * mm, "end": v(-6.23, 8.46) * mm});
            skLineSegment(sketch, "E67", {"start": v(-6.23, 8.46) * mm, "end": v(-3.88, 8.46) * mm});
            skLineSegment(sketch, "E68", {"start": v(-3.88, 8.46) * mm, "end": v(-3.88, 6.68) * mm});
            skLineSegment(sketch, "E69", {"start": v(-3.88, 6.68) * mm, "end": v(-6.23, 4.01) * mm});
            skLineSegment(sketch, "E70", {"start": v(-6.23, 4.01) * mm, "end": v(-9.34, 4.01) * mm});
            skLineSegment(sketch, "E71", {"start": v(-9.34, 16.11) * mm, "end": v(-9.34, -18.13) * mm, "construction": true});
            skPoint(sketch, "E71.endSnap0", {"position": v(-9.34, -9.76) * mm});
            skLineSegment(sketch, "E72.0", {"start": v(-3.88, 16.11) * mm, "end": v(-3.88, -18.13) * mm, "construction": true});
            skLineSegment(sketch, "E73.MirrorCS", {"start": v(-13.59, 10.24) * mm, "end": v(-12.45, 8.66) * mm});
            skLineSegment(sketch, "E74.MirrorCS", {"start": v(-12.45, 8.66) * mm, "end": v(-12.45, 8.46) * mm});
            skLineSegment(sketch, "E75.MirrorCS", {"start": v(-12.45, 8.46) * mm, "end": v(-14.8, 8.46) * mm});
            skLineSegment(sketch, "E76.MirrorCS", {"start": v(-14.8, 16.11) * mm, "end": v(-14.8, -18.13) * mm, "construction": true});
            skLineSegment(sketch, "E77.MirrorCS", {"start": v(-14.8, 6.68) * mm, "end": v(-12.45, 4.01) * mm});
            skLineSegment(sketch, "E78.MirrorCS", {"start": v(-12.45, 4.01) * mm, "end": v(-9.34, 4.01) * mm});
            skLineSegment(sketch, "E79.MirrorCS", {"start": v(-14.8, 8.46) * mm, "end": v(-14.8, 6.68) * mm});
            skLineSegment(sketch, "E80.1.0", {"start": v(-13.12, 3.35) * mm, "end": v(-13.12, 0.24) * mm});
            skLineSegment(sketch, "E80.1.1", {"start": v(-13.12, -2.87) * mm, "end": v(-13.12, 0.24) * mm});
            skLineSegment(sketch, "E80.1.2", {"start": v(-15.79, -5.22) * mm, "end": v(-13.12, -2.87) * mm});
            skLineSegment(sketch, "E80.1.3", {"start": v(-17.56, 3.35) * mm, "end": v(-17.56, 5.7) * mm});
            skLineSegment(sketch, "E80.1.4", {"start": v(-19.34, 4.48) * mm, "end": v(-17.77, 3.35) * mm});
            skLineSegment(sketch, "E80.1.5", {"start": v(-17.56, 5.7) * mm, "end": v(-15.79, 5.7) * mm});
            skLineSegment(sketch, "E80.1.6", {"start": v(-19.34, -4) * mm, "end": v(-17.77, -2.87) * mm});
            skLineSegment(sketch, "E80.1.7", {"start": v(-15.79, 5.7) * mm, "end": v(-13.12, 3.35) * mm});
            skLineSegment(sketch, "E80.1.8", {"start": v(-17.56, -5.22) * mm, "end": v(-15.79, -5.22) * mm});
            skLineSegment(sketch, "E80.1.9", {"start": v(-17.56, -2.87) * mm, "end": v(-17.56, -5.22) * mm});
            skLineSegment(sketch, "E80.1.10", {"start": v(-17.77, -2.87) * mm, "end": v(-17.56, -2.87) * mm});
            skLineSegment(sketch, "E80.1.11", {"start": v(-17.77, 3.35) * mm, "end": v(-17.56, 3.35) * mm});
            skLineSegment(sketch, "E80.2.0", {"start": v(-12.45, -3.54) * mm, "end": v(-9.34, -3.54) * mm});
            skLineSegment(sketch, "E80.2.1", {"start": v(-6.23, -3.54) * mm, "end": v(-9.34, -3.54) * mm});
            skLineSegment(sketch, "E80.2.2", {"start": v(-3.88, -6.2) * mm, "end": v(-6.23, -3.54) * mm});
            skLineSegment(sketch, "E80.2.3", {"start": v(-12.45, -7.98) * mm, "end": v(-14.8, -7.98) * mm});
            skLineSegment(sketch, "E80.2.4", {"start": v(-13.59, -9.76) * mm, "end": v(-12.45, -8.19) * mm});
            skLineSegment(sketch, "E80.2.5", {"start": v(-14.8, -7.98) * mm, "end": v(-14.8, -6.2) * mm});
            skLineSegment(sketch, "E80.2.6", {"start": v(-5.1, -9.76) * mm, "end": v(-6.23, -8.19) * mm});
            skLineSegment(sketch, "E80.2.7", {"start": v(-14.8, -6.2) * mm, "end": v(-12.45, -3.54) * mm});
            skLineSegment(sketch, "E80.2.8", {"start": v(-3.88, -7.98) * mm, "end": v(-3.88, -6.2) * mm});
            skLineSegment(sketch, "E80.2.9", {"start": v(-6.23, -7.98) * mm, "end": v(-3.88, -7.98) * mm});
            skLineSegment(sketch, "E80.2.10", {"start": v(-6.23, -8.19) * mm, "end": v(-6.23, -7.98) * mm});
            skLineSegment(sketch, "E80.2.11", {"start": v(-12.45, -8.19) * mm, "end": v(-12.45, -7.98) * mm});
            skLineSegment(sketch, "E80.3.0", {"start": v(-5.56, -2.87) * mm, "end": v(-5.56, 0.24) * mm});
            skLineSegment(sketch, "E80.3.1", {"start": v(-5.56, 3.35) * mm, "end": v(-5.56, 0.24) * mm});
            skLineSegment(sketch, "E80.3.2", {"start": v(-2.9, 5.7) * mm, "end": v(-5.56, 3.35) * mm});
            skLineSegment(sketch, "E80.3.3", {"start": v(-1.12, -2.87) * mm, "end": v(-1.12, -5.22) * mm});
            skLineSegment(sketch, "E80.3.4", {"start": v(0.66, -4) * mm, "end": v(-0.92, -2.87) * mm});
            skLineSegment(sketch, "E80.3.5", {"start": v(-1.12, -5.22) * mm, "end": v(-2.9, -5.22) * mm});
            skLineSegment(sketch, "E80.3.6", {"start": v(0.66, 4.48) * mm, "end": v(-0.92, 3.35) * mm});
            skLineSegment(sketch, "E80.3.7", {"start": v(-2.9, -5.22) * mm, "end": v(-5.56, -2.87) * mm});
            skLineSegment(sketch, "E80.3.8", {"start": v(-1.12, 5.7) * mm, "end": v(-2.9, 5.7) * mm});
            skLineSegment(sketch, "E80.3.9", {"start": v(-1.12, 3.35) * mm, "end": v(-1.12, 5.7) * mm});
            skLineSegment(sketch, "E80.3.10", {"start": v(-0.92, 3.35) * mm, "end": v(-1.12, 3.35) * mm});
            skLineSegment(sketch, "E80.3.11", {"start": v(-0.92, -2.87) * mm, "end": v(-1.12, -2.87) * mm});
            skLineSegment(sketch, "E81.bottom", {"start": v(20.66, -9.76) * mm, "end": v(0.66, -9.76) * mm});
            skLineSegment(sketch, "E81.top", {"start": v(20.66, 10.24) * mm, "end": v(0.66, 10.24) * mm});
            skLineSegment(sketch, "E81.left", {"start": v(20.66, -9.76) * mm, "end": v(20.66, 10.24) * mm});
            skPoint(sketch, "E81.middle", {"position": v(10.66, 0.24) * mm});
            skLineSegment(sketch, "E82", {"start": v(14.9, 10.24) * mm, "end": v(13.77, 8.66) * mm});
            skLineSegment(sketch, "E83", {"start": v(13.77, 8.66) * mm, "end": v(13.77, 8.46) * mm});
            skLineSegment(sketch, "E84", {"start": v(13.77, 8.46) * mm, "end": v(16.12, 8.46) * mm});
            skLineSegment(sketch, "E85", {"start": v(16.12, 8.46) * mm, "end": v(16.12, 6.68) * mm});
            skLineSegment(sketch, "E86", {"start": v(16.12, 6.68) * mm, "end": v(13.77, 4.01) * mm});
            skLineSegment(sketch, "E87", {"start": v(13.77, 4.01) * mm, "end": v(10.66, 4.01) * mm});
            skPoint(sketch, "E88.endSnap0", {"position": v(10.66, -9.76) * mm});
            skLineSegment(sketch, "E89.MirrorCS", {"start": v(6.41, 10.24) * mm, "end": v(7.55, 8.66) * mm});
            skLineSegment(sketch, "E90.MirrorCS", {"start": v(7.55, 8.66) * mm, "end": v(7.55, 8.46) * mm});
            skLineSegment(sketch, "E91.MirrorCS", {"start": v(7.55, 8.46) * mm, "end": v(5.2, 8.46) * mm});
            skLineSegment(sketch, "E92.MirrorCS", {"start": v(5.2, 6.68) * mm, "end": v(7.55, 4.01) * mm});
            skLineSegment(sketch, "E93.MirrorCS", {"start": v(7.55, 4.01) * mm, "end": v(10.66, 4.01) * mm});
            skLineSegment(sketch, "E94.MirrorCS", {"start": v(5.2, 8.46) * mm, "end": v(5.2, 6.68) * mm});
            skLineSegment(sketch, "E95.1.0", {"start": v(6.88, 3.35) * mm, "end": v(6.88, 0.24) * mm});
            skLineSegment(sketch, "E95.1.1", {"start": v(6.88, -2.87) * mm, "end": v(6.88, 0.24) * mm});
            skLineSegment(sketch, "E95.1.2", {"start": v(4.21, -5.22) * mm, "end": v(6.88, -2.87) * mm});
            skLineSegment(sketch, "E95.1.3", {"start": v(2.44, 3.35) * mm, "end": v(2.44, 5.7) * mm});
            skLineSegment(sketch, "E95.1.4", {"start": v(0.66, 4.48) * mm, "end": v(2.23, 3.35) * mm});
            skLineSegment(sketch, "E95.1.5", {"start": v(2.44, 5.7) * mm, "end": v(4.21, 5.7) * mm});
            skLineSegment(sketch, "E95.1.6", {"start": v(0.66, -4) * mm, "end": v(2.23, -2.87) * mm});
            skLineSegment(sketch, "E95.1.7", {"start": v(4.21, 5.7) * mm, "end": v(6.88, 3.35) * mm});
            skLineSegment(sketch, "E95.1.8", {"start": v(2.44, -5.22) * mm, "end": v(4.21, -5.22) * mm});
            skLineSegment(sketch, "E95.1.9", {"start": v(2.44, -2.87) * mm, "end": v(2.44, -5.22) * mm});
            skLineSegment(sketch, "E95.1.10", {"start": v(2.23, -2.87) * mm, "end": v(2.44, -2.87) * mm});
            skLineSegment(sketch, "E95.1.11", {"start": v(2.23, 3.35) * mm, "end": v(2.44, 3.35) * mm});
            skLineSegment(sketch, "E95.2.0", {"start": v(7.55, -3.54) * mm, "end": v(10.66, -3.54) * mm});
            skLineSegment(sketch, "E95.2.1", {"start": v(13.77, -3.54) * mm, "end": v(10.66, -3.54) * mm});
            skLineSegment(sketch, "E95.2.2", {"start": v(16.12, -6.2) * mm, "end": v(13.77, -3.54) * mm});
            skLineSegment(sketch, "E95.2.3", {"start": v(7.55, -7.98) * mm, "end": v(5.2, -7.98) * mm});
            skLineSegment(sketch, "E95.2.4", {"start": v(6.41, -9.76) * mm, "end": v(7.55, -8.19) * mm});
            skLineSegment(sketch, "E95.2.5", {"start": v(5.2, -7.98) * mm, "end": v(5.2, -6.2) * mm});
            skLineSegment(sketch, "E95.2.6", {"start": v(14.9, -9.76) * mm, "end": v(13.77, -8.19) * mm});
            skLineSegment(sketch, "E95.2.7", {"start": v(5.2, -6.2) * mm, "end": v(7.55, -3.54) * mm});
            skLineSegment(sketch, "E95.2.8", {"start": v(16.12, -7.98) * mm, "end": v(16.12, -6.2) * mm});
            skLineSegment(sketch, "E95.2.9", {"start": v(13.77, -7.98) * mm, "end": v(16.12, -7.98) * mm});
            skLineSegment(sketch, "E95.2.10", {"start": v(13.77, -8.19) * mm, "end": v(13.77, -7.98) * mm});
            skLineSegment(sketch, "E95.2.11", {"start": v(7.55, -8.19) * mm, "end": v(7.55, -7.98) * mm});
            skLineSegment(sketch, "E95.3.0", {"start": v(14.44, -2.87) * mm, "end": v(14.44, 0.24) * mm});
            skLineSegment(sketch, "E95.3.1", {"start": v(14.44, 3.35) * mm, "end": v(14.44, 0.24) * mm});
            skLineSegment(sketch, "E95.3.2", {"start": v(17.1, 5.7) * mm, "end": v(14.44, 3.35) * mm});
            skLineSegment(sketch, "E95.3.3", {"start": v(18.88, -2.87) * mm, "end": v(18.88, -5.22) * mm});
            skLineSegment(sketch, "E95.3.4", {"start": v(20.66, -4) * mm, "end": v(19.08, -2.87) * mm});
            skLineSegment(sketch, "E95.3.5", {"start": v(18.88, -5.22) * mm, "end": v(17.1, -5.22) * mm});
            skLineSegment(sketch, "E95.3.6", {"start": v(20.66, 4.48) * mm, "end": v(19.08, 3.35) * mm});
            skLineSegment(sketch, "E95.3.7", {"start": v(17.1, -5.22) * mm, "end": v(14.44, -2.87) * mm});
            skLineSegment(sketch, "E95.3.8", {"start": v(18.88, 5.7) * mm, "end": v(17.1, 5.7) * mm});
            skLineSegment(sketch, "E95.3.9", {"start": v(18.88, 3.35) * mm, "end": v(18.88, 5.7) * mm});
            skLineSegment(sketch, "E95.3.10", {"start": v(19.08, 3.35) * mm, "end": v(18.88, 3.35) * mm});
            skLineSegment(sketch, "E95.3.11", {"start": v(19.08, -2.87) * mm, "end": v(18.88, -2.87) * mm});
            skSolve(sketch);
        }
        {
            var Q0;
            {var subQ3=sQuery(id+"F6.wireOp",EDGE,"E65");Q0=makeQuery(id+"F6.imprint","IMPRINT",FACE,{"disambiguationData":[TD([[makeQuery(id+"F6.imprint","IMPRINT",EDGE,{"derivedFrom":subQ3}),1.0]])]});}
            var Q1;
            {var subQ4=sQuery(id+"F6.wireOp",EDGE,"E82");Q1=makeQuery(id+"F6.imprint","IMPRINT",FACE,{"disambiguationData":[TD([[makeQuery(id+"F6.imprint","IMPRINT",EDGE,{"derivedFrom":subQ4}),1.0]])]});}
            extrude(context, id + "F7", {"entities" : qUnion([Q0, Q1]), "depth" : 400 * mm, "symmetric" : true});
        }
        {
            var Q0;
            Q0=qCreatedBy(makeId("Right.planeOp"),FACE);
            var sketch = newSketch(context, id + "F8", { "sketchPlane" : qUnion([Q0])});
            skLineSegment(sketch, "E96.0", {"start": v(-56.93, 7.96) * mm, "end": v(-56.93, 7.96) * mm});
            skLineSegment(sketch, "E96.1", {"start": v(-56.93, 7.96) * mm, "end": v(-54.58, 7.96) * mm});
            skLineSegment(sketch, "E96.2", {"start": v(-54.58, 7.96) * mm, "end": v(-54.58, 6.87) * mm});
            skLineSegment(sketch, "E96.3", {"start": v(-54.58, 6.87) * mm, "end": v(-56.66, 4.51) * mm});
            skLineSegment(sketch, "E96.4", {"start": v(-56.66, 4.51) * mm, "end": v(-62.43, 4.51) * mm});
            skLineSegment(sketch, "E96.5", {"start": v(-62.15, 7.96) * mm, "end": v(-62.15, 7.96) * mm});
            skLineSegment(sketch, "E96.6", {"start": v(-62.15, 7.96) * mm, "end": v(-64.5, 7.96) * mm});
            skLineSegment(sketch, "E96.7", {"start": v(-64.5, 7.96) * mm, "end": v(-64.5, 6.87) * mm});
            skLineSegment(sketch, "E96.8", {"start": v(-64.5, 6.87) * mm, "end": v(-62.43, 4.51) * mm});
            skLineSegment(sketch, "E97", {"start": v(-62.15, 7.96) * mm, "end": v(-56.93, 7.96) * mm});
            skSolve(sketch);
        }
        {
            var Q0;
            Q0=makeQuery(id+"F8.imprint","IMPRINT",FACE,{"disambiguationData":[TD([[makeQuery(id+"F8.imprint","IMPRINT",EDGE,{"derivedFrom":sQuery(id+"F8.wireOp",EDGE,"E96.1")}),-1.0]])]});
            extrude(context, id + "F9", {"entities" : qUnion([Q0]), "depth" : 5.9 * mm});
        }
        {
            var Q0;
            Q0=makeQuery(id+"F9.opExtrude","SWEPT_FACE",FACE,{"disambiguationData":[OSD([sQuery(id+"F8.wireOp",EDGE,"E96.1"),sQuery(id+"F8.wireOp",EDGE,"E96.6"),sQuery(id+"F8.wireOp",EDGE,"E97")])]});
            var sketch = newSketch(context, id + "F10", { "sketchPlane" : qUnion([Q0])});
            skCircle(sketch, "E98", {"center": v(2.95, -59.54) * mm, "radius": 2.5 * mm});
            skLineSegment(sketch, "E99", {"start": v(0, -64.5) * mm, "end": v(5.9, -54.58) * mm, "construction": true});
            skSolve(sketch);
        }
        {
            var Q0;
            Q0=makeQuery(id+"F10.imprint","IMPRINT",FACE,{"disambiguationData":[TD([[makeQuery(id+"F10.imprint","IMPRINT",EDGE,{"derivedFrom":sQuery(id+"F10.wireOp",EDGE,"E98")}),1.0]])]});
            extrude(context, id + "F11", {"entities" : qUnion([Q0]), "operationType" : NewBodyOperationType.ADD, "depth" : 1 * mm});
        }
        {
            var Q0;
            Q0=makeQuery(id+"F11.opExtrude","CAP_FACE",FACE,{"disambiguationData":[OSD([sQuery(id+"F10.wireOp",EDGE,"E98")])],"isStart":false});
            var sketch = newSketch(context, id + "F12", { "sketchPlane" : qUnion([Q0])});
            skCircle(sketch, "E100", {"center": v(2.95, -59.54) * mm, "radius": 1.6 * mm});
            skSolve(sketch);
        }
        {
            var Q0;
            Q0=makeQuery(id+"F12.imprint","IMPRINT",FACE,{"disambiguationData":[TD([[makeQuery(id+"F12.imprint","IMPRINT",EDGE,{"derivedFrom":sQuery(id+"F12.wireOp",EDGE,"E100")}),1.0]])]});
            extrude(context, id + "F13", {"entities" : qUnion([Q0]), "operationType" : NewBodyOperationType.REMOVE, "endBound" : BoundingType.UP_TO_NEXT, "oppositeDirection" : true, "depth" : 25 * mm});
        }
        {
            var Q0;
            Q0=makeQuery(id+"F9.opExtrude","SWEPT_BODY",BODY,{"disambiguationData":[OSD([sQuery(id+"F8.wireOp",EDGE,"E96.1"),sQuery(id+"F8.wireOp",EDGE,"E96.2"),sQuery(id+"F8.wireOp",EDGE,"E96.3"),sQuery(id+"F8.wireOp",EDGE,"E96.4"),sQuery(id+"F8.wireOp",EDGE,"E96.6"),sQuery(id+"F8.wireOp",EDGE,"E96.7"),sQuery(id+"F8.wireOp",EDGE,"E96.8"),sQuery(id+"F8.wireOp",EDGE,"E97")])]});
            transform(context, id + "F14", {"entities" : qUnion([Q0]), "transformType" : TransformType.TRANSLATION_3D, "dx" : 0 * mm, "dy" : 0 * mm, "dz" : 0 * mm, "makeCopy" : true});
        }
    });
